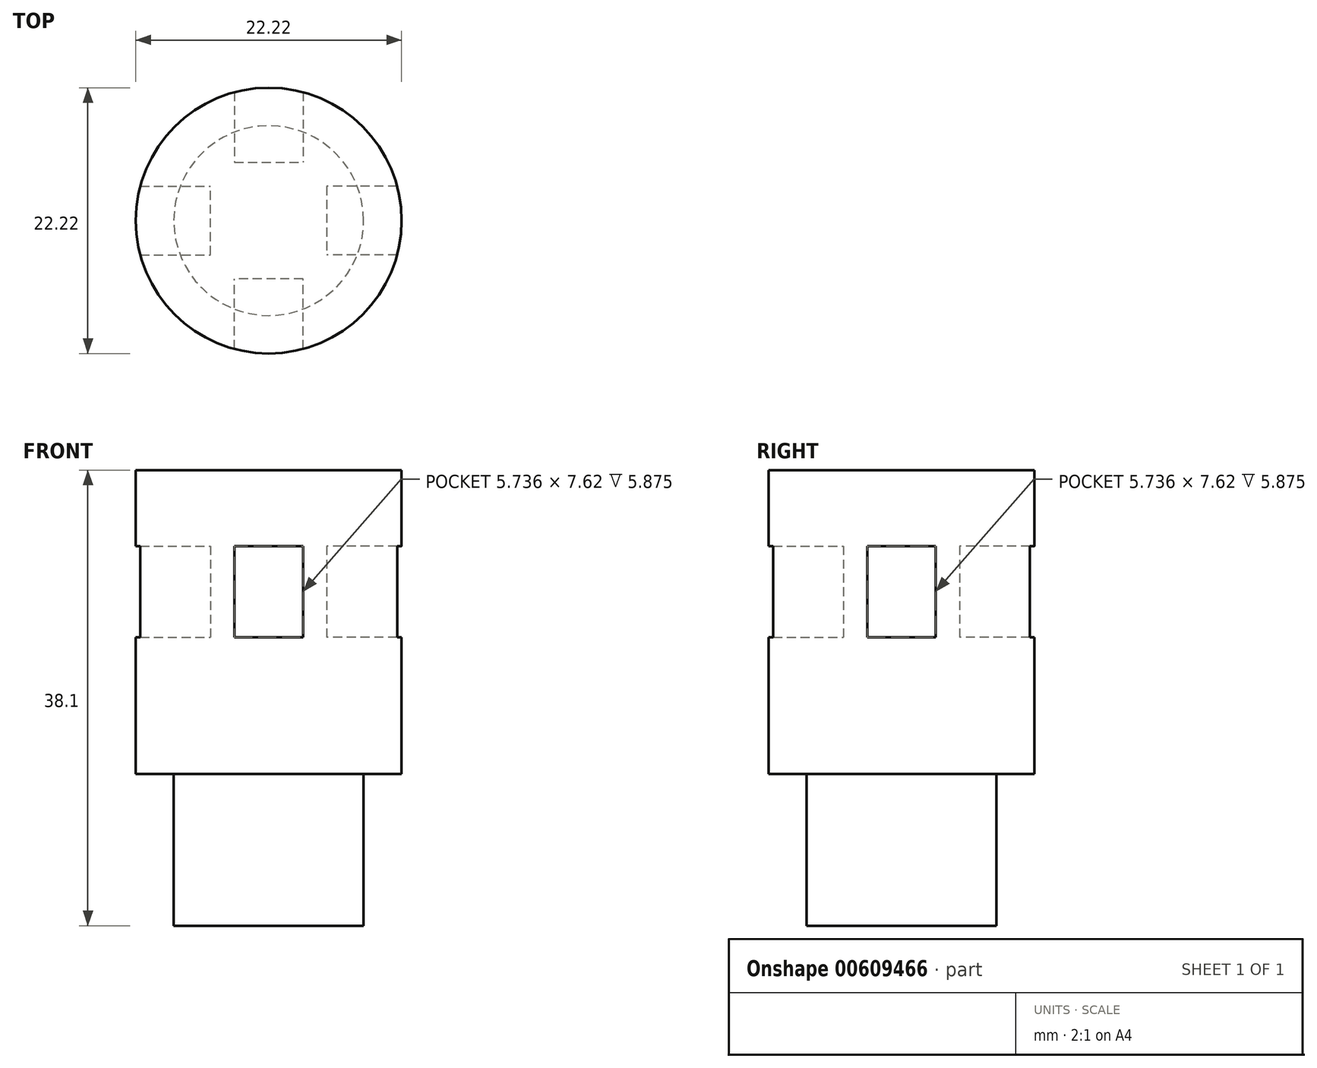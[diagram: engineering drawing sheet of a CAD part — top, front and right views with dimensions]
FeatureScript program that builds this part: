
annotation { "Feature Type Name" : "Feature", "Feature Type Description" : "" }
export const myFeature = defineFeature(function(context is Context, id is Id, definition is map)
    precondition{}
    {
        {
            var Q0;
            Q0=qCreatedBy(makeId("Top.planeOp"),FACE);
            var sketch = newSketch(context, id + "F0", { "sketchPlane" : qUnion([Q0])});
            skCircle(sketch, "E0", {"center": v(0, 0) * mm, "radius": 7.94 * mm});
            skCircle(sketch, "E1", {"center": v(0, 0) * mm, "radius": 11.11 * mm});
            skLineSegment(sketch, "E2", {"start": v(-2.87, 10.74) * mm, "end": v(2.87, 10.74) * mm});
            skLineSegment(sketch, "E3", {"start": v(0, 11.11) * mm, "end": v(0, 0) * mm});
            skPoint(sketch, "E4", {"position": v(0, 10.74) * mm});
            skLineSegment(sketch, "E5", {"start": v(-2.87, 10.74) * mm, "end": v(-2.87, 7.4) * mm});
            skLineSegment(sketch, "E6", {"start": v(2.87, 10.74) * mm, "end": v(2.87, 7.4) * mm});
            skLineSegment(sketch, "E7.1.0", {"start": v(-10.74, -2.87) * mm, "end": v(-7.4, -2.87) * mm});
            skLineSegment(sketch, "E7.1.1", {"start": v(-10.74, -2.87) * mm, "end": v(-10.74, 2.87) * mm});
            skLineSegment(sketch, "E7.1.2", {"start": v(-10.74, 2.87) * mm, "end": v(-7.4, 2.87) * mm});
            skLineSegment(sketch, "E7.2.0", {"start": v(2.87, -10.74) * mm, "end": v(2.87, -7.4) * mm});
            skLineSegment(sketch, "E7.2.1", {"start": v(2.87, -10.74) * mm, "end": v(-2.87, -10.74) * mm});
            skLineSegment(sketch, "E7.2.2", {"start": v(-2.87, -10.74) * mm, "end": v(-2.87, -7.4) * mm});
            skLineSegment(sketch, "E7.3.0", {"start": v(10.74, 2.87) * mm, "end": v(7.4, 2.87) * mm});
            skLineSegment(sketch, "E7.3.1", {"start": v(10.74, 2.87) * mm, "end": v(10.74, -2.87) * mm});
            skLineSegment(sketch, "E7.3.2", {"start": v(10.74, -2.87) * mm, "end": v(7.4, -2.87) * mm});
            skLineSegment(sketch, "E8", {"start": v(-2.87, 7.4) * mm, "end": v(-2.87, 4.86) * mm});
            skLineSegment(sketch, "E9", {"start": v(-2.87, 4.86) * mm, "end": v(2.87, 4.86) * mm});
            skLineSegment(sketch, "E10", {"start": v(2.87, 4.86) * mm, "end": v(2.87, 7.4) * mm});
            skLineSegment(sketch, "E11.1.0", {"start": v(-4.86, -2.87) * mm, "end": v(-4.86, 2.87) * mm});
            skLineSegment(sketch, "E11.1.1", {"start": v(-7.4, -2.87) * mm, "end": v(-4.86, -2.87) * mm});
            skLineSegment(sketch, "E11.1.2", {"start": v(-4.86, 2.87) * mm, "end": v(-7.4, 2.87) * mm});
            skLineSegment(sketch, "E11.2.0", {"start": v(2.87, -4.86) * mm, "end": v(-2.87, -4.86) * mm});
            skLineSegment(sketch, "E11.2.1", {"start": v(2.87, -7.4) * mm, "end": v(2.87, -4.86) * mm});
            skLineSegment(sketch, "E11.2.2", {"start": v(-2.87, -4.86) * mm, "end": v(-2.87, -7.4) * mm});
            skLineSegment(sketch, "E11.3.0", {"start": v(4.86, 2.87) * mm, "end": v(4.86, -2.87) * mm});
            skLineSegment(sketch, "E11.3.1", {"start": v(7.4, 2.87) * mm, "end": v(4.86, 2.87) * mm});
            skLineSegment(sketch, "E11.3.2", {"start": v(4.86, -2.87) * mm, "end": v(7.4, -2.87) * mm});
            skSolve(sketch);
        }
        {
            var Q0;
            {var subQ0=sQuery(id+"F0.wireOp",EDGE,"E5");Q0=makeQuery(id+"F0.imprint","IMPRINT",FACE,{"disambiguationData":[TD([[makeQuery(id+"F0.imprint","IMPRINT",EDGE,{"derivedFrom":subQ0}),-1.0]])]});}
            var Q1;
            {var subQ0=sQuery(id+"F0.wireOp",EDGE,"E6");Q1=makeQuery(id+"F0.imprint","IMPRINT",FACE,{"disambiguationData":[TD([[makeQuery(id+"F0.imprint","IMPRINT",EDGE,{"derivedFrom":subQ0}),1.0]])]});}
            var Q2;
            {var subQ0=sQuery(id+"F0.wireOp",EDGE,"E7.2.0");Q2=makeQuery(id+"F0.imprint","IMPRINT",FACE,{"disambiguationData":[TD([[makeQuery(id+"F0.imprint","IMPRINT",EDGE,{"derivedFrom":subQ0}),-1.0]])]});}
            var Q3;
            {var subQ0=sQuery(id+"F0.wireOp",EDGE,"E7.1.0");Q3=makeQuery(id+"F0.imprint","IMPRINT",FACE,{"disambiguationData":[TD([[makeQuery(id+"F0.imprint","IMPRINT",EDGE,{"derivedFrom":subQ0}),-1.0]])]});}
            var Q4;
            {var subQ0=sQuery(id+"F0.wireOp",EDGE,"E7.1.1");Q4=makeQuery(id+"F0.imprint","IMPRINT",FACE,{"disambiguationData":[TD([[makeQuery(id+"F0.imprint","IMPRINT",EDGE,{"derivedFrom":subQ0}),1.0]])]});}
            var Q5;
            {var subQ0=sQuery(id+"F0.wireOp",EDGE,"E7.1.0");Q5=makeQuery(id+"F0.imprint","IMPRINT",FACE,{"disambiguationData":[TD([[makeQuery(id+"F0.imprint","IMPRINT",EDGE,{"derivedFrom":subQ0}),1.0]])]});}
            var Q6;
            {var subQ0=sQuery(id+"F0.wireOp",EDGE,"E5");Q6=makeQuery(id+"F0.imprint","IMPRINT",FACE,{"disambiguationData":[TD([[makeQuery(id+"F0.imprint","IMPRINT",EDGE,{"derivedFrom":subQ0}),1.0]])]});}
            var Q7;
            {var subQ0=sQuery(id+"F0.wireOp",EDGE,"E6");Q7=makeQuery(id+"F0.imprint","IMPRINT",FACE,{"disambiguationData":[TD([[makeQuery(id+"F0.imprint","IMPRINT",EDGE,{"derivedFrom":subQ0}),-1.0]])]});}
            var Q8;
            {var subQ1=sQuery(id+"F0.wireOp",EDGE,"E1");var subQ3=sQuery(id+"F0.wireOp",EDGE,"E3");var subQ4=makeQuery(id+"F0.imprint","INTERSECT",VERTEX,{"derivedFrom":[subQ1,subQ3]});Q8=makeQuery(id+"F0.imprint","IMPRINT",FACE,{"disambiguationData":[TD([[makeQuery(id+"F0.imprint","IMPRINT",EDGE,{"disambiguationData":[TD([[subQ4,-1.0]])],"derivedFrom":subQ3}),1.0]])]});}
            var Q9;
            {var subQ1=sQuery(id+"F0.wireOp",EDGE,"E1");var subQ3=sQuery(id+"F0.wireOp",EDGE,"E3");var subQ4=makeQuery(id+"F0.imprint","INTERSECT",VERTEX,{"derivedFrom":[subQ1,subQ3]});Q9=makeQuery(id+"F0.imprint","IMPRINT",FACE,{"disambiguationData":[TD([[makeQuery(id+"F0.imprint","IMPRINT",EDGE,{"disambiguationData":[TD([[subQ4,-1.0]])],"derivedFrom":subQ3}),-1.0]])]});}
            var Q10;
            {var subQ0=sQuery(id+"F0.wireOp",EDGE,"E7.3.0");Q10=makeQuery(id+"F0.imprint","IMPRINT",FACE,{"disambiguationData":[TD([[makeQuery(id+"F0.imprint","IMPRINT",EDGE,{"derivedFrom":subQ0}),1.0]])]});}
            var Q11;
            {var subQ0=sQuery(id+"F0.wireOp",EDGE,"E7.3.1");Q11=makeQuery(id+"F0.imprint","IMPRINT",FACE,{"disambiguationData":[TD([[makeQuery(id+"F0.imprint","IMPRINT",EDGE,{"derivedFrom":subQ0}),1.0]])]});}
            var Q12;
            {var subQ0=sQuery(id+"F0.wireOp",EDGE,"E7.2.0");Q12=makeQuery(id+"F0.imprint","IMPRINT",FACE,{"disambiguationData":[TD([[makeQuery(id+"F0.imprint","IMPRINT",EDGE,{"derivedFrom":subQ0}),1.0]])]});}
            var Q13;
            {var subQ0=sQuery(id+"F0.wireOp",EDGE,"E7.2.1");Q13=makeQuery(id+"F0.imprint","IMPRINT",FACE,{"disambiguationData":[TD([[makeQuery(id+"F0.imprint","IMPRINT",EDGE,{"derivedFrom":subQ0}),1.0]])]});}
            var Q14;
            {var subQ0=sQuery(id+"F0.wireOp",EDGE,"E0");var subQ4=makeQuery(id+"F0.imprint","INTERSECT",VERTEX,{"derivedFrom":[subQ0,sQuery(id+"F0.wireOp",EDGE,"E6")]});Q14=makeQuery(id+"F0.imprint","IMPRINT",FACE,{"disambiguationData":[TD([[makeQuery(id+"F0.imprint","IMPRINT",EDGE,{"disambiguationData":[TD([[subQ4,1.0]])],"derivedFrom":subQ0}),1.0]])]});}
            var Q15;
            Q15=makeQuery(id+"F0.imprint","IMPRINT",FACE,{"disambiguationData":[TD([[makeQuery(id+"F0.imprint","IMPRINT",EDGE,{"derivedFrom":sQuery(id+"F0.wireOp",EDGE,"E11.3.0")}),1.0]])]});
            var Q16;
            {var subQ0=sQuery(id+"F0.wireOp",EDGE,"E8");Q16=makeQuery(id+"F0.imprint","IMPRINT",FACE,{"disambiguationData":[TD([[makeQuery(id+"F0.imprint","IMPRINT",EDGE,{"derivedFrom":subQ0}),1.0]])]});}
            var Q17;
            Q17=makeQuery(id+"F0.imprint","IMPRINT",FACE,{"disambiguationData":[TD([[makeQuery(id+"F0.imprint","IMPRINT",EDGE,{"derivedFrom":sQuery(id+"F0.wireOp",EDGE,"E11.1.0")}),1.0]])]});
            var Q18;
            {var subQ0=sQuery(id+"F0.wireOp",EDGE,"E10");Q18=makeQuery(id+"F0.imprint","IMPRINT",FACE,{"disambiguationData":[TD([[makeQuery(id+"F0.imprint","IMPRINT",EDGE,{"derivedFrom":subQ0}),1.0]])]});}
            var Q19;
            Q19=makeQuery(id+"F0.imprint","IMPRINT",FACE,{"disambiguationData":[TD([[makeQuery(id+"F0.imprint","IMPRINT",EDGE,{"derivedFrom":sQuery(id+"F0.wireOp",EDGE,"E11.2.0")}),1.0]])]});
            extrude(context, id + "F1", {"entities" : qUnion([Q0, Q1, Q2, Q3, Q4, Q5, Q6, Q7, Q8, Q9, Q10, Q11, Q12, Q13, Q14, Q15, Q16, Q17, Q18, Q19]), "depth" : 25.4 * mm, "offsetDistance" : 25.4 * mm});
        }
        {
            var Q0;
            {var subQ0=sQuery(id+"F0.wireOp",EDGE,"E7.2.1");Q0=makeQuery(id+"F0.imprint","IMPRINT",FACE,{"disambiguationData":[TD([[makeQuery(id+"F0.imprint","IMPRINT",EDGE,{"derivedFrom":subQ0}),1.0]])]});}
            var Q1;
            {var subQ0=sQuery(id+"F0.wireOp",EDGE,"E7.2.0");Q1=makeQuery(id+"F0.imprint","IMPRINT",FACE,{"disambiguationData":[TD([[makeQuery(id+"F0.imprint","IMPRINT",EDGE,{"derivedFrom":subQ0}),1.0]])]});}
            var Q2;
            {var subQ0=sQuery(id+"F0.wireOp",EDGE,"E7.1.0");Q2=makeQuery(id+"F0.imprint","IMPRINT",FACE,{"disambiguationData":[TD([[makeQuery(id+"F0.imprint","IMPRINT",EDGE,{"derivedFrom":subQ0}),1.0]])]});}
            var Q3;
            {var subQ0=sQuery(id+"F0.wireOp",EDGE,"E7.1.1");Q3=makeQuery(id+"F0.imprint","IMPRINT",FACE,{"disambiguationData":[TD([[makeQuery(id+"F0.imprint","IMPRINT",EDGE,{"derivedFrom":subQ0}),1.0]])]});}
            var Q4;
            {var subQ0=sQuery(id+"F0.wireOp",EDGE,"E7.3.0");Q4=makeQuery(id+"F0.imprint","IMPRINT",FACE,{"disambiguationData":[TD([[makeQuery(id+"F0.imprint","IMPRINT",EDGE,{"derivedFrom":subQ0}),1.0]])]});}
            var Q5;
            {var subQ0=sQuery(id+"F0.wireOp",EDGE,"E7.3.1");Q5=makeQuery(id+"F0.imprint","IMPRINT",FACE,{"disambiguationData":[TD([[makeQuery(id+"F0.imprint","IMPRINT",EDGE,{"derivedFrom":subQ0}),1.0]])]});}
            var Q6;
            {var subQ0=sQuery(id+"F0.wireOp",EDGE,"E6");Q6=makeQuery(id+"F0.imprint","IMPRINT",FACE,{"disambiguationData":[TD([[makeQuery(id+"F0.imprint","IMPRINT",EDGE,{"derivedFrom":subQ0}),-1.0]])]});}
            var Q7;
            {var subQ1=sQuery(id+"F0.wireOp",EDGE,"E1");var subQ3=sQuery(id+"F0.wireOp",EDGE,"E3");var subQ4=makeQuery(id+"F0.imprint","INTERSECT",VERTEX,{"derivedFrom":[subQ1,subQ3]});Q7=makeQuery(id+"F0.imprint","IMPRINT",FACE,{"disambiguationData":[TD([[makeQuery(id+"F0.imprint","IMPRINT",EDGE,{"disambiguationData":[TD([[subQ4,-1.0]])],"derivedFrom":subQ3}),1.0]])]});}
            var Q8;
            {var subQ0=sQuery(id+"F0.wireOp",EDGE,"E5");Q8=makeQuery(id+"F0.imprint","IMPRINT",FACE,{"disambiguationData":[TD([[makeQuery(id+"F0.imprint","IMPRINT",EDGE,{"derivedFrom":subQ0}),1.0]])]});}
            var Q9;
            {var subQ1=sQuery(id+"F0.wireOp",EDGE,"E1");var subQ3=sQuery(id+"F0.wireOp",EDGE,"E3");var subQ4=makeQuery(id+"F0.imprint","INTERSECT",VERTEX,{"derivedFrom":[subQ1,subQ3]});Q9=makeQuery(id+"F0.imprint","IMPRINT",FACE,{"disambiguationData":[TD([[makeQuery(id+"F0.imprint","IMPRINT",EDGE,{"disambiguationData":[TD([[subQ4,-1.0]])],"derivedFrom":subQ3}),-1.0]])]});}
            var Q10;
            Q10=makeQuery(id+"F0.imprint","IMPRINT",FACE,{"disambiguationData":[TD([[makeQuery(id+"F0.imprint","IMPRINT",EDGE,{"derivedFrom":sQuery(id+"F0.wireOp",EDGE,"E11.2.0")}),1.0]])]});
            var Q11;
            Q11=makeQuery(id+"F0.imprint","IMPRINT",FACE,{"disambiguationData":[TD([[makeQuery(id+"F0.imprint","IMPRINT",EDGE,{"derivedFrom":sQuery(id+"F0.wireOp",EDGE,"E11.1.0")}),1.0]])]});
            var Q12;
            {var subQ0=sQuery(id+"F0.wireOp",EDGE,"E8");Q12=makeQuery(id+"F0.imprint","IMPRINT",FACE,{"disambiguationData":[TD([[makeQuery(id+"F0.imprint","IMPRINT",EDGE,{"derivedFrom":subQ0}),1.0]])]});}
            var Q13;
            {var subQ0=sQuery(id+"F0.wireOp",EDGE,"E10");Q13=makeQuery(id+"F0.imprint","IMPRINT",FACE,{"disambiguationData":[TD([[makeQuery(id+"F0.imprint","IMPRINT",EDGE,{"derivedFrom":subQ0}),1.0]])]});}
            var Q14;
            Q14=makeQuery(id+"F0.imprint","IMPRINT",FACE,{"disambiguationData":[TD([[makeQuery(id+"F0.imprint","IMPRINT",EDGE,{"derivedFrom":sQuery(id+"F0.wireOp",EDGE,"E11.3.0")}),1.0]])]});
            extrude(context, id + "F2", {"entities" : qUnion([Q0, Q1, Q2, Q3, Q4, Q5, Q6, Q7, Q8, Q9, Q10, Q11, Q12, Q13, Q14]), "operationType" : NewBodyOperationType.REMOVE, "depth" : 19.05 * mm, "offsetDistance" : 25.4 * mm, "hasSecondDirection" : true, "secondDirectionOppositeDirection" : false, "secondDirectionDepth" : 11.43 * mm});
        }
        {
            var Q0;
            {var subQ3=sQuery(id+"F0.wireOp",EDGE,"E8");Q0=makeQuery(id+"F0.imprint","IMPRINT",FACE,{"disambiguationData":[TD([[makeQuery(id+"F0.imprint","IMPRINT",EDGE,{"derivedFrom":subQ3}),-1.0]])]});}
            var Q1;
            Q1=makeQuery(id+"F0.imprint","IMPRINT",FACE,{"disambiguationData":[TD([[makeQuery(id+"F0.imprint","IMPRINT",EDGE,{"derivedFrom":sQuery(id+"F0.wireOp",EDGE,"E11.2.0")}),1.0]])]});
            var Q2;
            Q2=makeQuery(id+"F0.imprint","IMPRINT",FACE,{"disambiguationData":[TD([[makeQuery(id+"F0.imprint","IMPRINT",EDGE,{"derivedFrom":sQuery(id+"F0.wireOp",EDGE,"E11.3.0")}),1.0]])]});
            var Q3;
            {var subQ0=sQuery(id+"F0.wireOp",EDGE,"E10");Q3=makeQuery(id+"F0.imprint","IMPRINT",FACE,{"disambiguationData":[TD([[makeQuery(id+"F0.imprint","IMPRINT",EDGE,{"derivedFrom":subQ0}),1.0]])]});}
            var Q4;
            {var subQ0=sQuery(id+"F0.wireOp",EDGE,"E8");Q4=makeQuery(id+"F0.imprint","IMPRINT",FACE,{"disambiguationData":[TD([[makeQuery(id+"F0.imprint","IMPRINT",EDGE,{"derivedFrom":subQ0}),1.0]])]});}
            var Q5;
            Q5=makeQuery(id+"F0.imprint","IMPRINT",FACE,{"disambiguationData":[TD([[makeQuery(id+"F0.imprint","IMPRINT",EDGE,{"derivedFrom":sQuery(id+"F0.wireOp",EDGE,"E11.1.0")}),1.0]])]});
            extrude(context, id + "F3", {"entities" : qUnion([Q0, Q1, Q2, Q3, Q4, Q5]), "operationType" : NewBodyOperationType.ADD, "oppositeDirection" : true, "depth" : 12.7 * mm, "offsetDistance" : 25.4 * mm});
        }
    });
